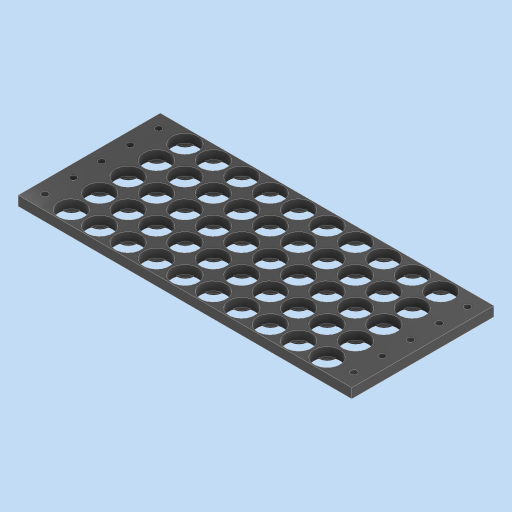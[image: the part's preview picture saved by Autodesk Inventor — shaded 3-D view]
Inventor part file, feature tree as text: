
AUTODESK INVENTOR PART (.ipt)
format: ipt  version: 2023 (Build 270158000, 158)  size: 12,494,336 bytes
history: native  units: in
note: dims shown in document units (in); Inventor stores cm internally (conversion verified against a paired STEP export)
features: extrude x3, sketch x2, other x1, pattern_linear x1
ambient origin geometry x8: Origin, YZ Plane, XZ Plane, XY Plane, X Axis, Y Axis, Z Axis, Center Point
bodies: Solid1 (feature_tree)
feature tree (7):
  parser-record x1  (decoder bookkeeping rows leaked as tree rows — omitted from the tree; the rows remain in map.json)
  sketch  "Sketch1"  dims[d0=0.8268in d1=0.9055in]
  extrude  "Extrusion1"  Depth=0.9055in
  extrude  "Extrusion2"  Depth=0.3937in TaperAngle=360.0deg
  pattern_linear  "Rectangular Pattern1"  Spacing1=0.0315in  [1 undecoded]
  extrude  "Extrusion3"  Depth=0.9055in
  sketch  "Sketch2"  dims[d2=0.2756in d3=0.0in d4=1.5748in d6=360.0deg d8=0.0315in d9=0.0in d10=3.937in d12=0.9055in d13=1.9685in d15=0.9055in d16=0.7874in d17=0.2047in d18=0.3937in d19=0.0in d20=0.0197in d21=0.0344in d22=0.0197in d23=0.0344in]
note: 1 required parameter value undecoded (feature->parameter linkage not recoverable at this tier; creation-order binding heuristic only, values carry confidence <= 0.55)
note: 1 file-system path scrubbed to <path> (originals preserved in map.json)
